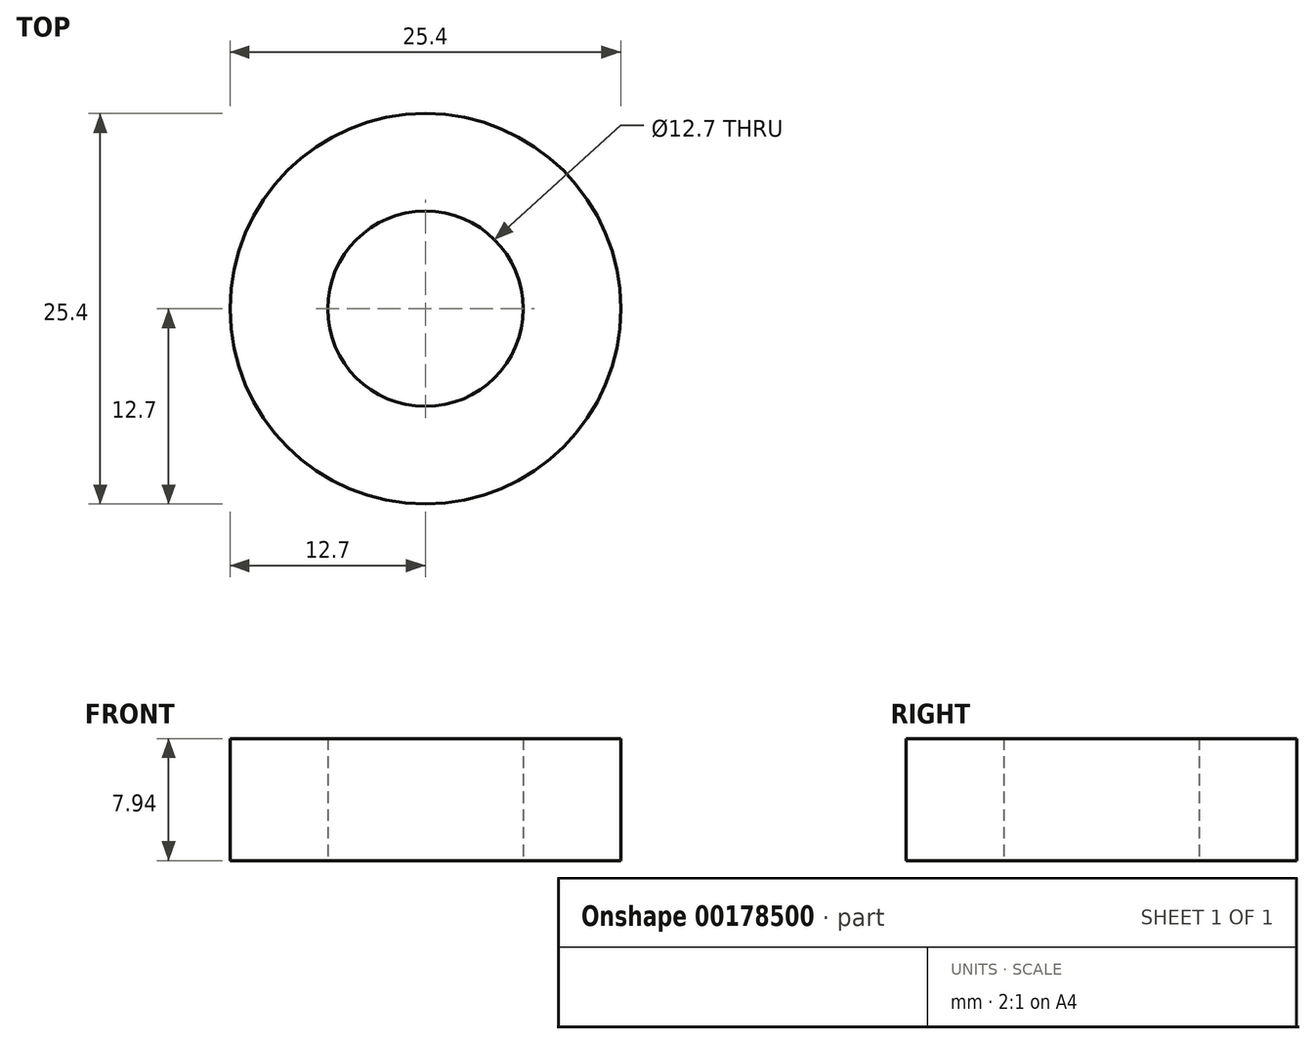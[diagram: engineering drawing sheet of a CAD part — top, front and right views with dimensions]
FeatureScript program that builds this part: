
annotation { "Feature Type Name" : "Feature", "Feature Type Description" : "" }
export const myFeature = defineFeature(function(context is Context, id is Id, definition is map)
    precondition{}
    {
        {
            var Q0;
            Q0=qCreatedBy(makeId("Top.planeOp"),FACE);
            var sketch = newSketch(context, id + "F0", { "sketchPlane" : qUnion([Q0])});
            skCircle(sketch, "E0", {"center": v(0, 0) * mm, "radius": 6.35 * mm});
            skCircle(sketch, "E1", {"center": v(0, 0) * mm, "radius": 12.7 * mm});
            skSolve(sketch);
        }
        {
            var Q0;
            Q0=makeQuery(id+"F0.imprint","IMPRINT",FACE,{"disambiguationData":[TD([[makeQuery(id+"F0.imprint","IMPRINT",EDGE,{"derivedFrom":sQuery(id+"F0.wireOp",EDGE,"E0")}),-1.0]])]});
            extrude(context, id + "F1", {"entities" : qUnion([Q0]), "depth" : 7.94 * mm});
        }
    });
